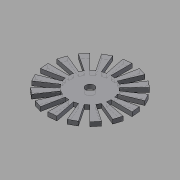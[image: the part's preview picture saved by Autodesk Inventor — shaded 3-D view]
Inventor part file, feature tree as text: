
AUTODESK INVENTOR PART (.ipt)
format: ipt  version: 2015 (Build 190159000, 159)  size: 173,568 bytes
history: native  units: in
note: dims shown in document units (in); Inventor stores cm internally (conversion verified against a paired STEP export)
features: other x3, sketch x1
ambient origin geometry x8: Origin, YZ Plane, XZ Plane, XY Plane, X Axis, Y Axis, Z Axis, Center Point
bodies: Solid1 (feature_tree)
feature tree (4):
  other  "encoder.ipt"
  other  "Solid2::encoder.ipt"
  other  "TaggingFeature1"
  sketch  "Sketch1"  dims[d0=0.3937in]
